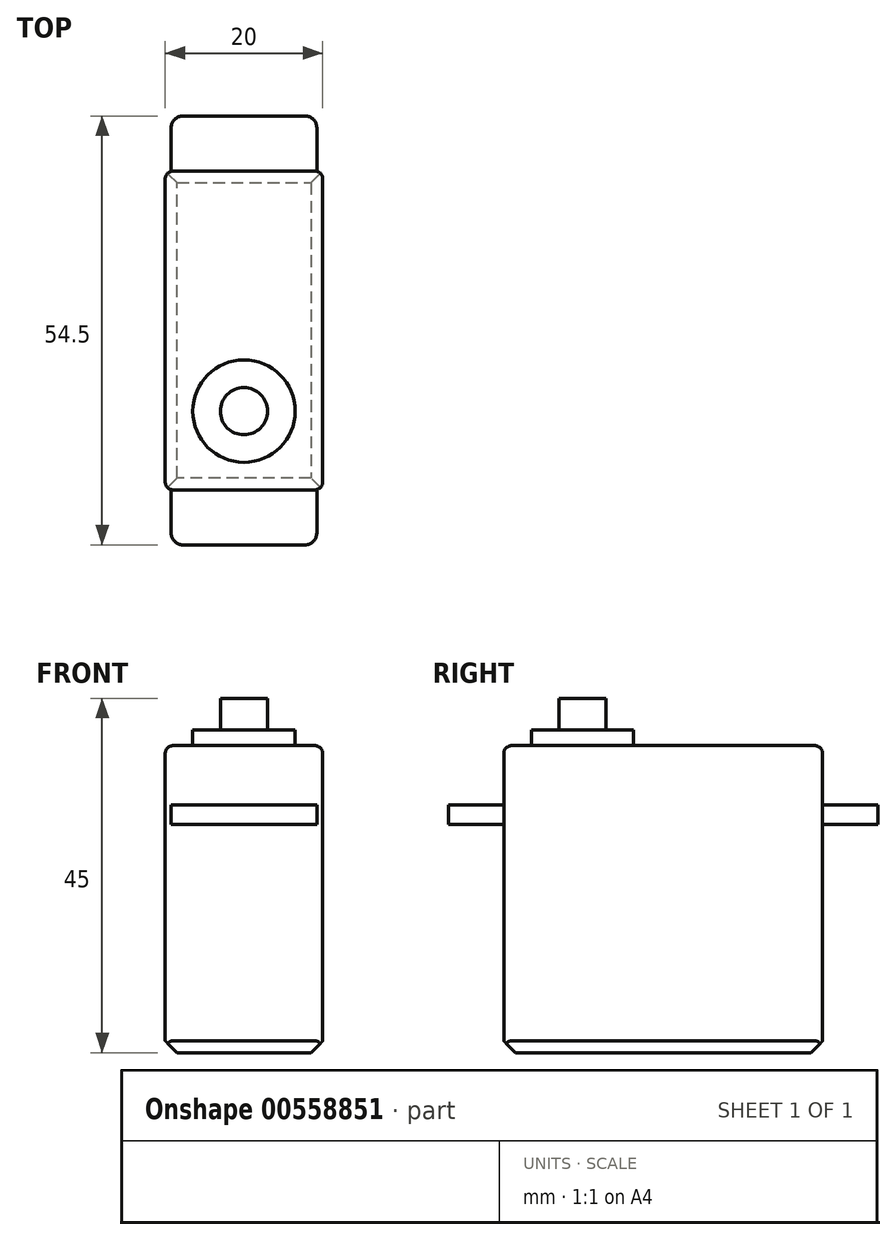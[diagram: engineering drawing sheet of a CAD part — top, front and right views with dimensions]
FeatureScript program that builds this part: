
annotation { "Feature Type Name" : "Feature", "Feature Type Description" : "" }
export const myFeature = defineFeature(function(context is Context, id is Id, definition is map)
    precondition{}
    {
        {
            var Q0;
            Q0=qCreatedBy(makeId("Top.planeOp"),FACE);
            var sketch = newSketch(context, id + "F0", { "sketchPlane" : qUnion([Q0])});
            skLineSegment(sketch, "E0.bottom", {"start": v(10, -20.25) * mm, "end": v(-10, -20.25) * mm});
            skLineSegment(sketch, "E0.top", {"start": v(10, 20.25) * mm, "end": v(-10, 20.25) * mm});
            skLineSegment(sketch, "E0.left", {"start": v(10, -20.25) * mm, "end": v(10, 20.25) * mm});
            skLineSegment(sketch, "E0.right", {"start": v(-10, -20.25) * mm, "end": v(-10, 20.25) * mm});
            skPoint(sketch, "E0.middle", {"position": v(0, 0) * mm});
            skLineSegment(sketch, "E1.bottom", {"start": v(7.75, 27.25) * mm, "end": v(-7.75, 27.25) * mm});
            skLineSegment(sketch, "E1.top", {"start": v(7.75, -27.25) * mm, "end": v(-7.75, -27.25) * mm});
            skLineSegment(sketch, "E1.left", {"start": v(9.25, 25.75) * mm, "end": v(9.25, -25.75) * mm});
            skLineSegment(sketch, "E1.right", {"start": v(-9.25, 25.75) * mm, "end": v(-9.25, -25.75) * mm});
            skPoint(sketch, "E2.visualSharp", {"position": v(-9.25, 27.25) * mm});
            skArc(sketch, "E2.filletArc", {"start": v(-7.75, 27.25) * mm, "mid": v(-8.81, 26.81) * mm, "end": v(-9.25, 25.75) * mm});
            skPoint(sketch, "E3.visualSharp", {"position": v(9.25, 27.25) * mm});
            skArc(sketch, "E3.filletArc", {"start": v(9.25, 25.75) * mm, "mid": v(8.81, 26.81) * mm, "end": v(7.75, 27.25) * mm});
            skPoint(sketch, "E4.visualSharp", {"position": v(-9.25, -27.25) * mm});
            skArc(sketch, "E4.filletArc", {"start": v(-9.25, -25.75) * mm, "mid": v(-8.81, -26.81) * mm, "end": v(-7.75, -27.25) * mm});
            skPoint(sketch, "E5.visualSharp", {"position": v(9.25, -27.25) * mm});
            skArc(sketch, "E5.filletArc", {"start": v(7.75, -27.25) * mm, "mid": v(8.81, -26.81) * mm, "end": v(9.25, -25.75) * mm});
            skSolve(sketch);
        }
        {
            var Q0;
            Q0=makeQuery(id+"F0.imprint","IMPRINT",FACE,{"disambiguationData":[TD([[makeQuery(id+"F0.imprint","IMPRINT",EDGE,{"derivedFrom":sQuery(id+"F0.wireOp",EDGE,"E0.bottom")}),-1.0]])]});
            extrude(context, id + "F1", {"entities" : qUnion([Q0]), "oppositeDirection" : true, "depth" : 29 * mm, "offsetDistance" : 25 * mm, "hasSecondDirection" : true, "secondDirectionOppositeDirection" : false, "secondDirectionDepth" : 10 * mm});
        }
        {
            var Q0;
            Q0=makeQuery(id+"F0.imprint","IMPRINT",FACE,{"disambiguationData":[TD([[makeQuery(id+"F0.imprint","IMPRINT",EDGE,{"derivedFrom":sQuery(id+"F0.wireOp",EDGE,"E1.top")}),-1.0]])]});
            var Q1;
            Q1=makeQuery(id+"F0.imprint","IMPRINT",FACE,{"disambiguationData":[TD([[makeQuery(id+"F0.imprint","IMPRINT",EDGE,{"derivedFrom":sQuery(id+"F0.wireOp",EDGE,"E1.bottom")}),1.0]])]});
            extrude(context, id + "F2", {"entities" : qUnion([Q0, Q1]), "operationType" : NewBodyOperationType.ADD, "depth" : 2.5 * mm, "offsetDistance" : 25 * mm});
        }
        {
            var Q0;
            Q0=makeQuery(id+"F1.opExtrude","CAP_FACE",FACE,{"disambiguationData":[OSD([sQuery(id+"F0.wireOp",EDGE,"E0.bottom"),sQuery(id+"F0.wireOp",EDGE,"E0.top"),sQuery(id+"F0.wireOp",EDGE,"E0.left"),sQuery(id+"F0.wireOp",EDGE,"E0.right")])],"isStart":true});
            var sketch = newSketch(context, id + "F3", { "sketchPlane" : qUnion([Q0])});
            skCircle(sketch, "E6", {"center": v(0, -10.25) * mm, "radius": 10 * mm});
            skCircle(sketch, "E7", {"center": v(0, -10.25) * mm, "radius": 6.5 * mm});
            skCircle(sketch, "E8", {"center": v(0, -10.25) * mm, "radius": 3 * mm});
            skSolve(sketch);
        }
        {
            var Q0;
            Q0=makeQuery(id+"F3.imprint","IMPRINT",FACE,{"disambiguationData":[TD([[makeQuery(id+"F3.imprint","IMPRINT",EDGE,{"derivedFrom":sQuery(id+"F3.wireOp",EDGE,"E7")}),1.0]])]});
            extrude(context, id + "F4", {"entities" : qUnion([Q0]), "operationType" : NewBodyOperationType.ADD, "depth" : 2 * mm, "offsetDistance" : 25 * mm});
        }
        {
            var Q0;
            Q0=makeQuery(id+"F3.imprint","IMPRINT",FACE,{"disambiguationData":[TD([[makeQuery(id+"F3.imprint","IMPRINT",EDGE,{"derivedFrom":sQuery(id+"F3.wireOp",EDGE,"E8")}),1.0]])]});
            extrude(context, id + "F5", {"entities" : qUnion([Q0]), "operationType" : NewBodyOperationType.ADD, "depth" : 6 * mm, "offsetDistance" : 25 * mm});
        }
        {
            var Q0;
            Q0=makeQuery(id+"F1.opExtrude","CAP_FACE",FACE,{"disambiguationData":[OSD([sQuery(id+"F0.wireOp",EDGE,"E0.bottom"),sQuery(id+"F0.wireOp",EDGE,"E0.top"),sQuery(id+"F0.wireOp",EDGE,"E0.left"),sQuery(id+"F0.wireOp",EDGE,"E0.right")])],"isStart":false});
            chamfer(context, id + "F6", {"entities" : qUnion([Q0]), "width" : 1.5 * mm, "tangentPropagation" : true});
        }
        {
            var Q0;
            Q0=makeQuery(id+"F1.opExtrude","CAP_EDGE",EDGE,{"disambiguationData":[OSD([sQuery(id+"F0.wireOp",EDGE,"E0.right")])],"isStart":true});
            var Q1;
            Q1=makeQuery(id+"F1.opExtrude","CAP_EDGE",EDGE,{"disambiguationData":[OSD([sQuery(id+"F0.wireOp",EDGE,"E0.top")])],"isStart":true});
            var Q2;
            Q2=makeQuery(id+"F1.opExtrude","CAP_EDGE",EDGE,{"disambiguationData":[OSD([sQuery(id+"F0.wireOp",EDGE,"E0.left")])],"isStart":true});
            var Q3;
            Q3=makeQuery(id+"F1.opExtrude","CAP_EDGE",EDGE,{"disambiguationData":[OSD([sQuery(id+"F0.wireOp",EDGE,"E0.bottom")])],"isStart":true});
            var Q4;
            Q4=makeQuery(id+"F1.opExtrude","SWEPT_EDGE",EDGE,{"disambiguationData":[OSD([sQuery(id+"F0.wireOp",EDGE,"E0.top"),sQuery(id+"F0.wireOp",EDGE,"E0.left")])]});
            var Q5;
            Q5=makeQuery(id+"F1.opExtrude","SWEPT_EDGE",EDGE,{"disambiguationData":[OSD([sQuery(id+"F0.wireOp",EDGE,"E0.bottom"),sQuery(id+"F0.wireOp",EDGE,"E0.right")])]});
            var Q6;
            Q6=makeQuery(id+"F1.opExtrude","SWEPT_EDGE",EDGE,{"disambiguationData":[OSD([sQuery(id+"F0.wireOp",EDGE,"E0.bottom"),sQuery(id+"F0.wireOp",EDGE,"E0.left")])]});
            var Q7;
            Q7=makeQuery(id+"F1.opExtrude","SWEPT_EDGE",EDGE,{"disambiguationData":[OSD([sQuery(id+"F0.wireOp",EDGE,"E0.top"),sQuery(id+"F0.wireOp",EDGE,"E0.right")])]});
            fillet(context, id + "F7", {"entities" : qUnion([Q0, Q1, Q2, Q3, Q4, Q5, Q6, Q7]), "radius" : 1 * mm, "tangentPropagation" : true, "allowEdgeOverflow" : false});
        }
    });
